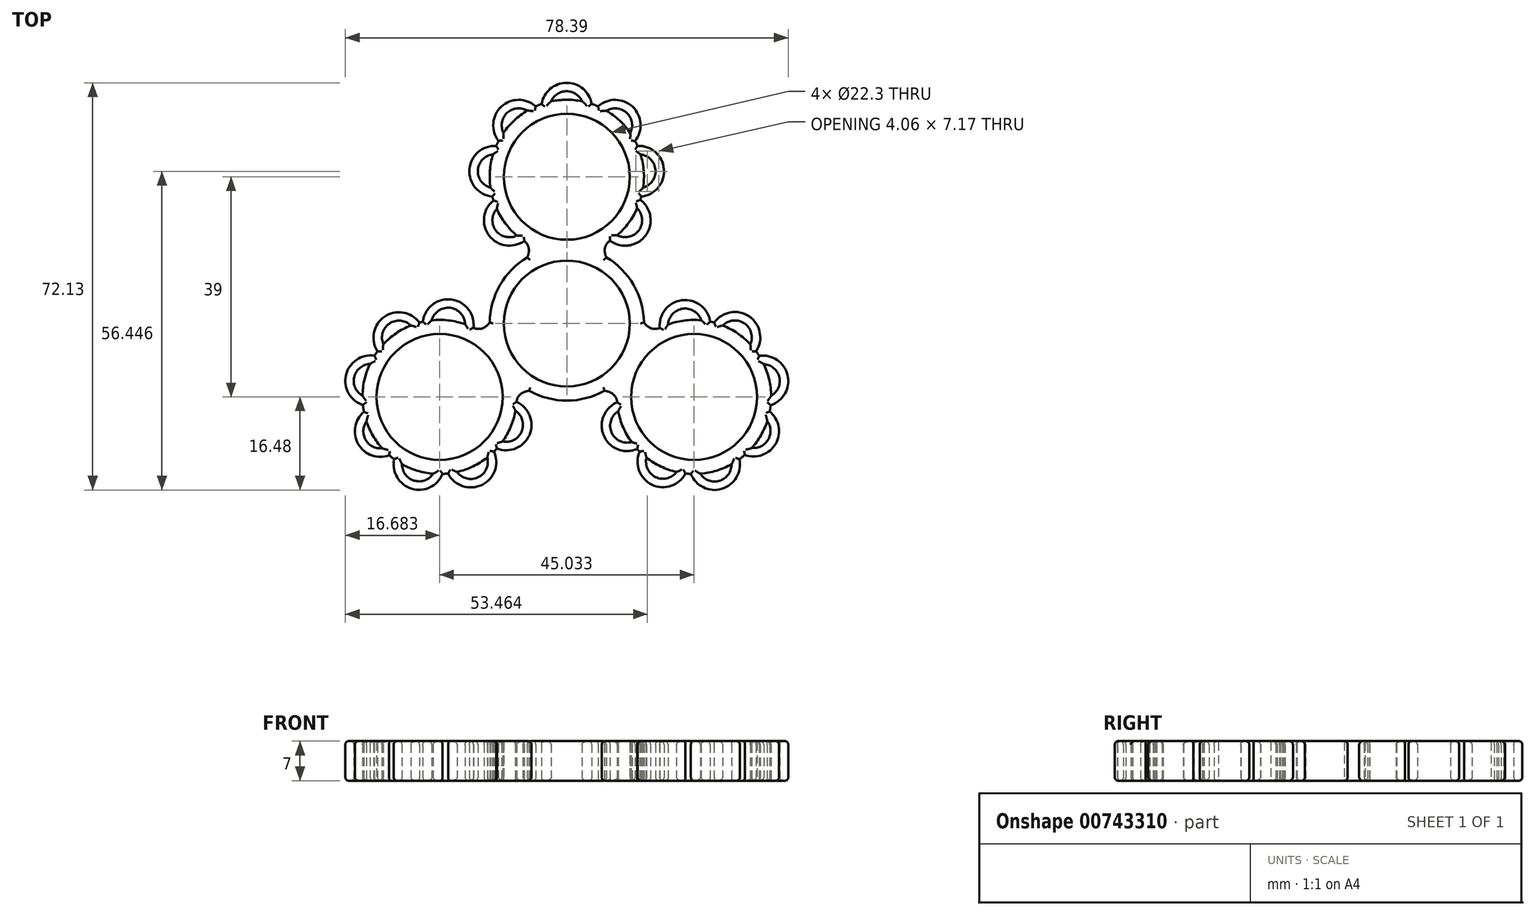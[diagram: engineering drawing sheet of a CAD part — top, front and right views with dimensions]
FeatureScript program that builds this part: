
annotation { "Feature Type Name" : "Feature", "Feature Type Description" : "" }
export const myFeature = defineFeature(function(context is Context, id is Id, definition is map)
    precondition{}
    {
        {
            var Q0;
            Q0=qCreatedBy(makeId("Top.planeOp"),FACE);
            var sketch = newSketch(context, id + "F0", { "sketchPlane" : qUnion([Q0])});
            skCircle(sketch, "E0", {"center": v(0, 0) * mm, "radius": 11.15 * mm});
            skArc(sketch, "E1.0", {"start": v(-5.17, 12.63) * mm, "mid": v(-6.92, 11.76) * mm, "end": v(-8.53, 10.66) * mm, "construction": true});
            skLineSegment(sketch, "E2", {"start": v(0, 0) * mm, "end": v(0, 26) * mm, "construction": true});
            skCircle(sketch, "E3", {"center": v(0, 26) * mm, "radius": 11.15 * mm});
            skArc(sketch, "E4.0", {"start": v(7, 14.28) * mm, "mid": v(0, 39.65) * mm, "end": v(-7, 14.28) * mm});
            skPoint(sketch, "E5.visualSharp", {"position": v(0, 16.7) * mm});
            skLineSegment(sketch, "E6.0", {"start": v(7, 0) * mm, "end": v(7, 29.5) * mm, "construction": true});
            skArc(sketch, "E7.trimOffspring", {"start": v(-7, 11.72) * mm, "mid": v(0, -13.65) * mm, "end": v(7, 11.72) * mm});
            skArc(sketch, "E8", {"start": v(7, 14.28) * mm, "mid": v(6.7, 13) * mm, "end": v(7, 11.72) * mm});
            skArc(sketch, "E9.MirrorCS", {"start": v(-7, 14.28) * mm, "mid": v(-6.7, 13) * mm, "end": v(-7, 11.72) * mm});
            skCircle(sketch, "E10", {"center": v(8.56, 35.13) * mm, "radius": 4.5 * mm});
            skCircle(sketch, "E11", {"center": v(-0.03, 38.15) * mm, "radius": 4.5 * mm});
            skCircle(sketch, "E12", {"center": v(-8.53, 35.13) * mm, "radius": 4.5 * mm});
            skCircle(sketch, "E13", {"center": v(-12.75, 26.98) * mm, "radius": 4.5 * mm});
            skCircle(sketch, "E14", {"center": v(12.7, 26.98) * mm, "radius": 4.5 * mm});
            skCircle(sketch, "E15", {"center": v(-0.03, 38.15) * mm, "radius": 3 * mm});
            skCircle(sketch, "E16", {"center": v(-8.53, 35.14) * mm, "radius": 3 * mm});
            skCircle(sketch, "E17", {"center": v(-12.75, 26.98) * mm, "radius": 3 * mm});
            skCircle(sketch, "E18", {"center": v(8.56, 35.14) * mm, "radius": 3 * mm});
            skCircle(sketch, "E19", {"center": v(12.7, 26.98) * mm, "radius": 3 * mm});
            skCircle(sketch, "E20", {"center": v(-10.17, 18.3) * mm, "radius": 4.5 * mm});
            skCircle(sketch, "E21", {"center": v(-10.17, 18.3) * mm, "radius": 3 * mm});
            skCircle(sketch, "E22", {"center": v(10.34, 18.3) * mm, "radius": 4.5 * mm});
            skCircle(sketch, "E23", {"center": v(10.34, 18.3) * mm, "radius": 3 * mm});
            skSolve(sketch);
        }
        {
            var Q0;
            Q0=qSketchRegion(id+"F2",true);
            var Q1;
            Q1=qSketchRegion(id+"F0",true);
            var Q2;
            {var subQ0=sQuery(id+"F0.wireOp",EDGE,"5286eaf0-ed28-4451-94e3-1d908ec19ca7");var subQ1=sQuery(id+"F0.wireOp",EDGE,"E3");var subQ2=makeQuery(id+"F0.imprint","INTERSECT",VERTEX,{"disambiguationData":[OD(0.0)],"derivedFrom":[subQ1,subQ0]});Q2=makeQuery(id+"F0.imprint","IMPRINT",FACE,{"disambiguationData":[TD([[makeQuery(id+"F0.imprint","IMPRINT",EDGE,{"disambiguationData":[TD([[subQ2,-1.0]])],"derivedFrom":subQ1}),-1.0]])]});}
            var Q3;
            {var subQ0=sQuery(id+"F0.wireOp",EDGE,"E17");var subQ1=sQuery(id+"F0.wireOp",EDGE,"E3");var subQ2=makeQuery(id+"F0.imprint","INTERSECT",VERTEX,{"disambiguationData":[OD(0.0)],"derivedFrom":[subQ1,subQ0]});Q3=makeQuery(id+"F0.imprint","IMPRINT",FACE,{"disambiguationData":[TD([[makeQuery(id+"F0.imprint","IMPRINT",EDGE,{"disambiguationData":[TD([[subQ2,-1.0]])],"derivedFrom":subQ1}),-1.0]])]});}
            var Q4;
            {var subQ0=sQuery(id+"F0.wireOp",EDGE,"E16");var subQ1=sQuery(id+"F0.wireOp",EDGE,"E3");var subQ2=makeQuery(id+"F0.imprint","INTERSECT",VERTEX,{"disambiguationData":[OD(0.0)],"derivedFrom":[subQ1,subQ0]});Q4=makeQuery(id+"F0.imprint","IMPRINT",FACE,{"disambiguationData":[TD([[makeQuery(id+"F0.imprint","IMPRINT",EDGE,{"disambiguationData":[TD([[subQ2,-1.0]])],"derivedFrom":subQ1}),-1.0]])]});}
            var Q5;
            {var subQ0=sQuery(id+"F0.wireOp",EDGE,"E15");var subQ1=sQuery(id+"F0.wireOp",EDGE,"E3");var subQ2=makeQuery(id+"F0.imprint","INTERSECT",VERTEX,{"disambiguationData":[OD(0.0)],"derivedFrom":[subQ1,subQ0]});Q5=makeQuery(id+"F0.imprint","IMPRINT",FACE,{"disambiguationData":[TD([[makeQuery(id+"F0.imprint","IMPRINT",EDGE,{"disambiguationData":[TD([[subQ2,-1.0]])],"derivedFrom":subQ1}),-1.0]])]});}
            var Q6;
            {var subQ0=sQuery(id+"F0.wireOp",EDGE,"E18");var subQ1=sQuery(id+"F0.wireOp",EDGE,"E3");var subQ2=makeQuery(id+"F0.imprint","INTERSECT",VERTEX,{"disambiguationData":[OD(0.0)],"derivedFrom":[subQ1,subQ0]});Q6=makeQuery(id+"F0.imprint","IMPRINT",FACE,{"disambiguationData":[TD([[makeQuery(id+"F0.imprint","IMPRINT",EDGE,{"disambiguationData":[TD([[subQ2,-1.0]])],"derivedFrom":subQ1}),-1.0]])]});}
            var Q7;
            {var subQ0=sQuery(id+"F0.wireOp",EDGE,"E19");var subQ1=sQuery(id+"F0.wireOp",EDGE,"E3");var subQ2=makeQuery(id+"F0.imprint","INTERSECT",VERTEX,{"disambiguationData":[OD(0.0)],"derivedFrom":[subQ1,subQ0]});Q7=makeQuery(id+"F0.imprint","IMPRINT",FACE,{"disambiguationData":[TD([[makeQuery(id+"F0.imprint","IMPRINT",EDGE,{"disambiguationData":[TD([[subQ2,1.0]])],"derivedFrom":subQ1}),-1.0]])]});}
            var Q8;
            {var subQ0=sQuery(id+"F0.wireOp",EDGE,"8457dc48-e8ce-439c-b6e1-438fe0c9034f");var subQ1=sQuery(id+"F0.wireOp",EDGE,"E3");var subQ2=makeQuery(id+"F0.imprint","INTERSECT",VERTEX,{"disambiguationData":[OD(0.0)],"derivedFrom":[subQ1,subQ0]});Q8=makeQuery(id+"F0.imprint","IMPRINT",FACE,{"disambiguationData":[TD([[makeQuery(id+"F0.imprint","IMPRINT",EDGE,{"disambiguationData":[TD([[subQ2,-1.0]])],"derivedFrom":subQ1}),-1.0]])]});}
            var Q9;
            {var subQ0=sQuery(id+"F0.wireOp",EDGE,"E21");var subQ1=sQuery(id+"F0.wireOp",EDGE,"E3");var subQ2=makeQuery(id+"F0.imprint","INTERSECT",VERTEX,{"disambiguationData":[OD(0.0)],"derivedFrom":[subQ1,subQ0]});Q9=makeQuery(id+"F0.imprint","IMPRINT",FACE,{"disambiguationData":[TD([[makeQuery(id+"F0.imprint","IMPRINT",EDGE,{"disambiguationData":[TD([[subQ2,-1.0]])],"derivedFrom":subQ1}),-1.0]])]});}
            var Q10;
            {var subQ0=sQuery(id+"F0.wireOp",EDGE,"E23");var subQ1=sQuery(id+"F0.wireOp",EDGE,"E3");var subQ2=makeQuery(id+"F0.imprint","INTERSECT",VERTEX,{"disambiguationData":[OD(0.0)],"derivedFrom":[subQ1,subQ0]});Q10=makeQuery(id+"F0.imprint","IMPRINT",FACE,{"disambiguationData":[TD([[makeQuery(id+"F0.imprint","IMPRINT",EDGE,{"disambiguationData":[TD([[subQ2,-1.0]])],"derivedFrom":subQ1}),-1.0]])]});}
            extrude(context, id + "F1", {"entities" : qUnion([Q0, Q1, Q2, Q3, Q4, Q5, Q6, Q7, Q8, Q9, Q10]), "depth" : 7 * mm, "offsetDistance" : 25 * mm});
        }
        {
            var Q0;
            Q0=qCreatedBy(makeId("Right.planeOp"),FACE);
            var sketch = newSketch(context, id + "F2", { "sketchPlane" : qUnion([Q0])});
            skLineSegment(sketch, "E24", {"start": v(0, -11.35) * mm, "end": v(0, 14.45) * mm, "construction": true});
            skSolve(sketch);
        }
        {
            var Q0;
            Q0=makeQuery(id+"F1.opExtrude","SWEPT_EDGE",EDGE,{"disambiguationData":[OSD([sQuery(id+"F0.wireOp",EDGE,"E4.0"),sQuery(id+"F0.wireOp",EDGE,"gXTc2K6m-pDrj-VkwX-DA3g-2FsoQV2dXgWA"),sQuery(id+"F0.wireOp",EDGE,"E8")])]});
            var Q1;
            Q1=makeQuery(id+"F1.opExtrude","SWEPT_EDGE",EDGE,{"disambiguationData":[OSD([sQuery(id+"F0.wireOp",EDGE,"E4.0"),sQuery(id+"F0.wireOp",EDGE,"WV1YJwpc-lhCt-Tkbw-pyGD-IAguLvoMxcio"),sQuery(id+"F0.wireOp",EDGE,"E9.MirrorCS")])]});
            fillet(context, id + "F3", {"entities" : qUnion([Q0, Q1]), "radius" : 2 * mm, "tangentPropagation" : true, "allowEdgeOverflow" : false});
        }
        {
            var Q0;
            Q0=makeQuery(id+"F1.opExtrude","SWEPT_FACE",FACE,{"disambiguationData":[OSD([sQuery(id+"F0.wireOp",EDGE,"E0")])]});
            var Q1;
            Q1=makeQuery(id+"F1.opExtrude","SWEPT_FACE",FACE,{"disambiguationData":[OSD([sQuery(id+"F0.wireOp",EDGE,"E3")])]});
            fillet(context, id + "F4", {"entities" : qUnion([Q0, Q1]), "radius" : 0.2 * mm, "tangentPropagation" : true, "allowEdgeOverflow" : false});
        }
        {
            var Q0;
            Q0=makeQuery(id+"F1.opExtrude","SWEPT_EDGE",EDGE,{"disambiguationData":[OSD([sQuery(id+"F0.wireOp",EDGE,"B6IW4b8f-rdPB-c0Us-c8Mo-Mq4TzhgtsJ4K"),sQuery(id+"F0.wireOp",EDGE,"YkMFX2vO-4Crt-TsgE-euFS-UGkuE4yFQV92")])]});
            var Q1;
            Q1=makeQuery(id+"F1.opExtrude","SWEPT_EDGE",EDGE,{"disambiguationData":[OSD([sQuery(id+"F0.wireOp",EDGE,"05Ssocvi-DhHh-OsZG-e2E6-rp3hOyrowWxE"),sQuery(id+"F0.wireOp",EDGE,"gXTc2K6m-pDrj-VkwX-DA3g-2FsoQV2dXgWA")])]});
            var Q2;
            Q2=makeQuery(id+"F1.opExtrude","SWEPT_EDGE",EDGE,{"disambiguationData":[OSD([sQuery(id+"F0.wireOp",EDGE,"WV1YJwpc-lhCt-Tkbw-pyGD-IAguLvoMxcio"),sQuery(id+"F0.wireOp",EDGE,"lRAOphcG-mkQV-B9rX-murS-RDVpryX3sv7Y")])]});
            var Q3;
            Q3=makeQuery(id+"F1.opExtrude","CAP_FACE",FACE,{"disambiguationData":[OSD([sQuery(id+"F0.wireOp",EDGE,"E0"),sQuery(id+"F0.wireOp",EDGE,"E3"),sQuery(id+"F0.wireOp",EDGE,"E4.0"),sQuery(id+"F0.wireOp",EDGE,"E7.trimOffspring"),sQuery(id+"F0.wireOp",EDGE,"E8"),sQuery(id+"F0.wireOp",EDGE,"E9.MirrorCS"),sQuery(id+"F0.wireOp",EDGE,"E10"),sQuery(id+"F0.wireOp",EDGE,"E11"),sQuery(id+"F0.wireOp",EDGE,"E12"),sQuery(id+"F0.wireOp",EDGE,"E13"),sQuery(id+"F0.wireOp",EDGE,"E14"),sQuery(id+"F0.wireOp",EDGE,"dd87b57e-f014-4439-b0ae-6b8a5318a583"),sQuery(id+"F0.wireOp",EDGE,"9d18db76-b666-4d6e-9b71-35c6185a29a1")])],"isStart":false});
            var Q4;
            Q4=makeQuery(id+"F1.opExtrude","CAP_FACE",FACE,{"disambiguationData":[OSD([sQuery(id+"F0.wireOp",EDGE,"E0"),sQuery(id+"F0.wireOp",EDGE,"E3"),sQuery(id+"F0.wireOp",EDGE,"E4.0"),sQuery(id+"F0.wireOp",EDGE,"E7.trimOffspring"),sQuery(id+"F0.wireOp",EDGE,"E8"),sQuery(id+"F0.wireOp",EDGE,"E9.MirrorCS"),sQuery(id+"F0.wireOp",EDGE,"E10"),sQuery(id+"F0.wireOp",EDGE,"E11"),sQuery(id+"F0.wireOp",EDGE,"E12"),sQuery(id+"F0.wireOp",EDGE,"E13"),sQuery(id+"F0.wireOp",EDGE,"E14"),sQuery(id+"F0.wireOp",EDGE,"dd87b57e-f014-4439-b0ae-6b8a5318a583"),sQuery(id+"F0.wireOp",EDGE,"9d18db76-b666-4d6e-9b71-35c6185a29a1")])],"isStart":true});
            fillet(context, id + "F5", {"entities" : qUnion([Q0, Q1, Q2, Q3, Q4]), "radius" : 0.6 * mm, "tangentPropagation" : true, "allowEdgeOverflow" : false});
        }
        {
            var Q0;
            Q0=makeQuery(id+"F1.opExtrude","SWEPT_BODY",BODY,{"disambiguationData":[OSD([sQuery(id+"F0.wireOp",EDGE,"E0"),sQuery(id+"F0.wireOp",EDGE,"E1.0"),sQuery(id+"F0.wireOp",EDGE,"E3"),sQuery(id+"F0.wireOp",EDGE,"E4.0"),sQuery(id+"F0.wireOp",EDGE,"7c884c8c-e37f-41f7-9a8e-9150e4511ce8.0"),sQuery(id+"F0.wireOp",EDGE,"124d70be-8a2f-4ff1-8067-023c3a760d13.0"),sQuery(id+"F0.wireOp",EDGE,"7qioyo7K-iHsX-Xa6s-X97m-BwtuQXfGrCvp"),sQuery(id+"F0.wireOp",EDGE,"oFAU7C9Q-nsB6-dseo-MMuZ-7hNLlDQCrwbt"),sQuery(id+"F0.wireOp",EDGE,"a2486781-22df-47b1-8026-fe576fbc433f.0"),sQuery(id+"F0.wireOp",EDGE,"cb9c9ce2-17e4-408e-8bf5-b38f411324f0.0"),sQuery(id+"F0.wireOp",EDGE,"jKmUo85i-UXFQ-YKQP-mafa-QPdGbBQ2pSZu"),sQuery(id+"F0.wireOp",EDGE,"14rnQz0T-OoW9-SuH9-BmvN-4Fd0IeYT7QfG")])]});
            var Q1;
            Q1=sQuery(id+"F2.wireOp",EDGE,"E24");
            circularPattern(context, id + "F6", {"operationType" : NewBodyOperationType.ADD, "entities" : qUnion([Q0]), "axis" : qUnion([Q1]), "angle" : 360 * degree, "instanceCount" : 3, "equalSpace" : true});
        }
    });
